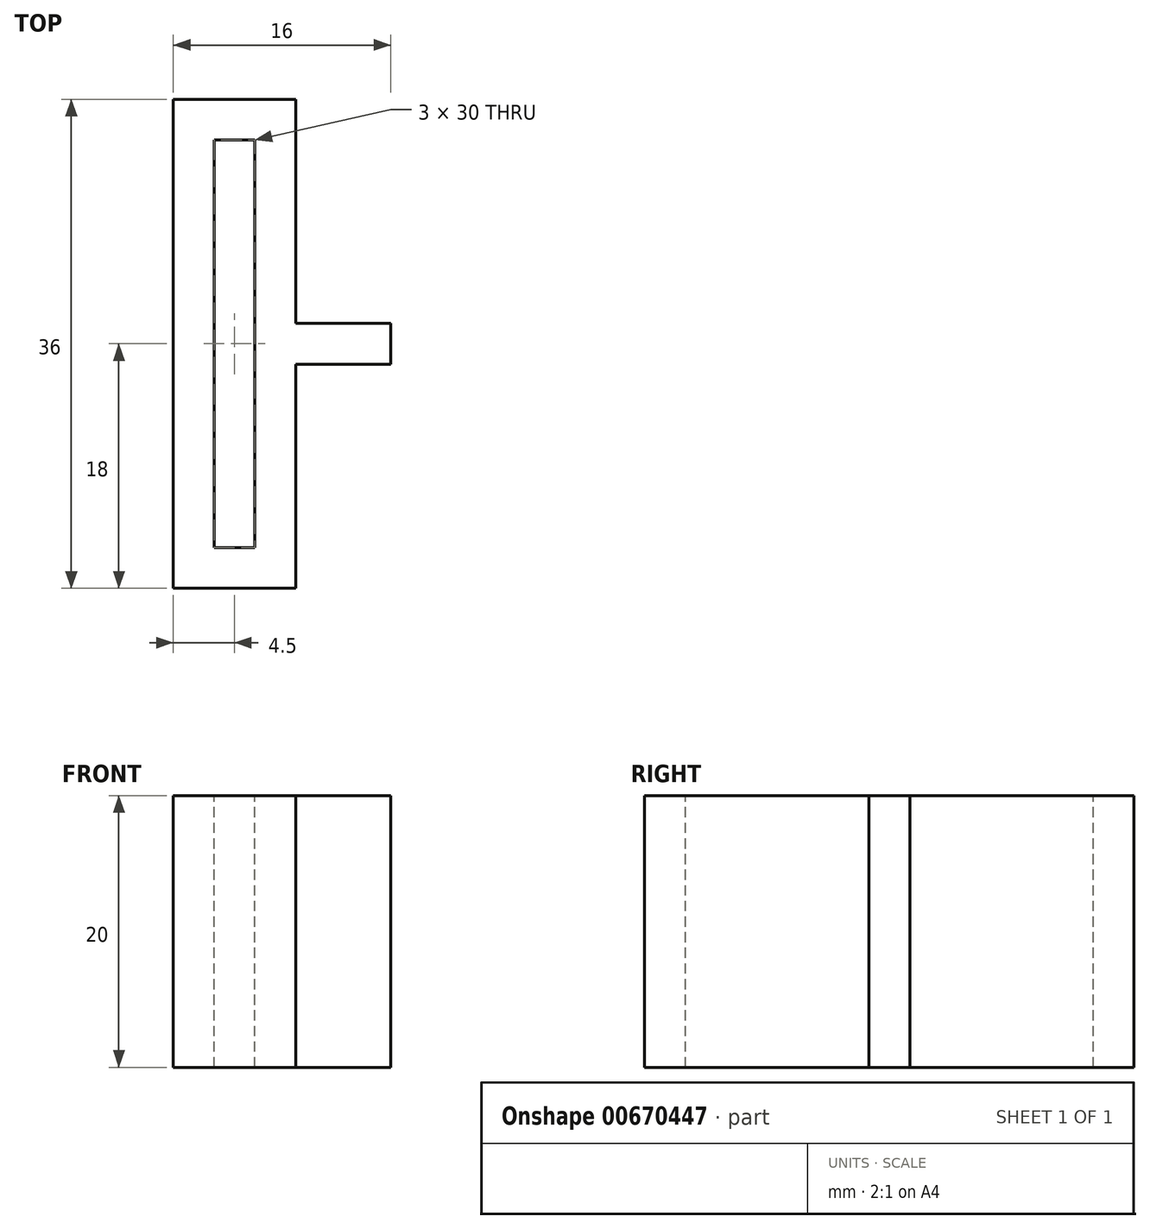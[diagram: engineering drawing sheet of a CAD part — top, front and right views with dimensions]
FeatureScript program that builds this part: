
annotation { "Feature Type Name" : "Feature", "Feature Type Description" : "" }
export const myFeature = defineFeature(function(context is Context, id is Id, definition is map)
    precondition{}
    {
        {
            var Q0;
            Q0=qCreatedBy(makeId("Top.planeOp"),FACE);
            var sketch = newSketch(context, id + "F0", { "sketchPlane" : qUnion([Q0])});
            skLineSegment(sketch, "E0", {"start": v(0, 0) * mm, "end": v(0, 36) * mm});
            skLineSegment(sketch, "E1", {"start": v(0, 36) * mm, "end": v(9, 36) * mm});
            skLineSegment(sketch, "E2", {"start": v(9, 36) * mm, "end": v(9, 19.5) * mm});
            skLineSegment(sketch, "E3", {"start": v(9, 19.5) * mm, "end": v(16, 19.5) * mm});
            skLineSegment(sketch, "E4", {"start": v(16, 19.5) * mm, "end": v(16, 16.5) * mm});
            skLineSegment(sketch, "E5", {"start": v(16, 16.5) * mm, "end": v(9, 16.5) * mm});
            skLineSegment(sketch, "E6", {"start": v(9, 16.5) * mm, "end": v(9, 0) * mm});
            skLineSegment(sketch, "E7", {"start": v(9, 0) * mm, "end": v(0, 0) * mm});
            skSolve(sketch);
        }
        {
            var Q0;
            Q0=makeQuery(id+"F0.imprint","IMPRINT",FACE,{"disambiguationData":[TD([[makeQuery(id+"F0.imprint","IMPRINT",EDGE,{"derivedFrom":sQuery(id+"F0.wireOp",EDGE,"E0")}),-1.0]])]});
            extrude(context, id + "F1", {"entities" : qUnion([Q0]), "depth" : 20 * mm, "offsetDistance" : 25 * mm});
        }
        {
            var Q0;
            Q0=makeQuery(id+"F1.opExtrude","CAP_FACE",FACE,{"disambiguationData":[OSD([sQuery(id+"F0.wireOp",EDGE,"E0"),sQuery(id+"F0.wireOp",EDGE,"E1"),sQuery(id+"F0.wireOp",EDGE,"E2"),sQuery(id+"F0.wireOp",EDGE,"E3"),sQuery(id+"F0.wireOp",EDGE,"E4"),sQuery(id+"F0.wireOp",EDGE,"E5"),sQuery(id+"F0.wireOp",EDGE,"E6"),sQuery(id+"F0.wireOp",EDGE,"E7")])],"isStart":false});
            var sketch = newSketch(context, id + "F2", { "sketchPlane" : qUnion([Q0])});
            skLineSegment(sketch, "E8.bottom", {"start": v(3, 33) * mm, "end": v(6, 33) * mm});
            skLineSegment(sketch, "E8.top", {"start": v(3, 3) * mm, "end": v(6, 3) * mm});
            skLineSegment(sketch, "E8.left", {"start": v(3, 33) * mm, "end": v(3, 3) * mm});
            skLineSegment(sketch, "E8.right", {"start": v(6, 33) * mm, "end": v(6, 3) * mm});
            skSolve(sketch);
        }
        {
            var Q0;
            Q0=makeQuery(id+"F2.imprint","IMPRINT",FACE,{"disambiguationData":[TD([[makeQuery(id+"F2.imprint","IMPRINT",EDGE,{"derivedFrom":sQuery(id+"F2.wireOp",EDGE,"E8.bottom")}),-1.0]])]});
            extrude(context, id + "F3", {"entities" : qUnion([Q0]), "operationType" : NewBodyOperationType.REMOVE, "endBound" : BoundingType.THROUGH_ALL, "oppositeDirection" : true, "depth" : 25 * mm, "offsetDistance" : 25 * mm});
        }
    });
